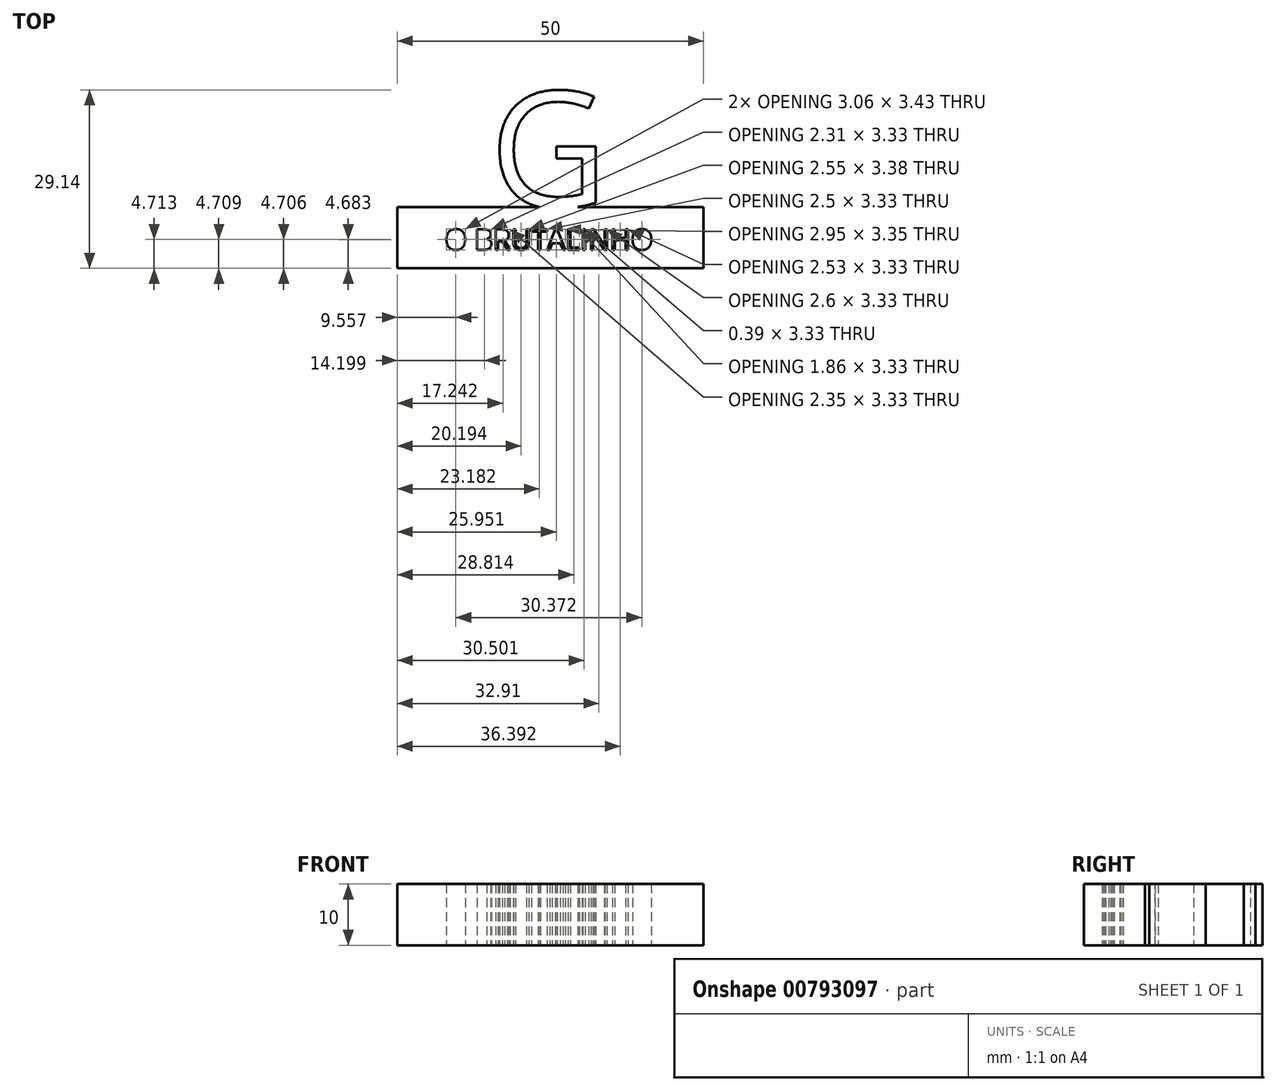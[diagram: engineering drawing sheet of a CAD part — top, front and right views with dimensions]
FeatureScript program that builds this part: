
annotation { "Feature Type Name" : "Feature", "Feature Type Description" : "" }
export const myFeature = defineFeature(function(context is Context, id is Id, definition is map)
    precondition{}
    {
        {
            var Q0;
            Q0=qCreatedBy(makeId("Top.planeOp"),FACE);
            var sketch = newSketch(context, id + "F0", { "sketchPlane" : qUnion([Q0])});
            skLineSegment(sketch, "E0.bottom", {"start": v(0, 0) * mm, "end": v(50, 0) * mm});
            skLineSegment(sketch, "E0.top", {"start": v(0, 10) * mm, "end": v(50, 10) * mm});
            skLineSegment(sketch, "E0.left", {"start": v(0, 0) * mm, "end": v(0, 10) * mm});
            skLineSegment(sketch, "E0.right", {"start": v(50, 0) * mm, "end": v(50, 10) * mm});
            skText(sketch, "E1", { "text": "O BRUTALINHO", "fontName": "OpenSans-Regular.ttf"});
            skText(sketch, "E2", { "text": "G", "fontName": "OpenSans-Regular.ttf"});
            const initialGuessF0  = {"E1": [0.00774, 0.00304, 1, 0, 0.00336], "E2": [0.01508, 0.01, 1, 0, 0.01903]};
            skSetInitialGuess(sketch, initialGuessF0);
            skSolve(sketch);
        }
        {
            var Q0;
            Q0 = qSketchRegion(id + "F0", true);
            extrude(context, id + "F1", {"entities" : qUnion([Q0]), "depth" : 10 * mm, "offsetDistance" : 25 * mm});
        }
    });
